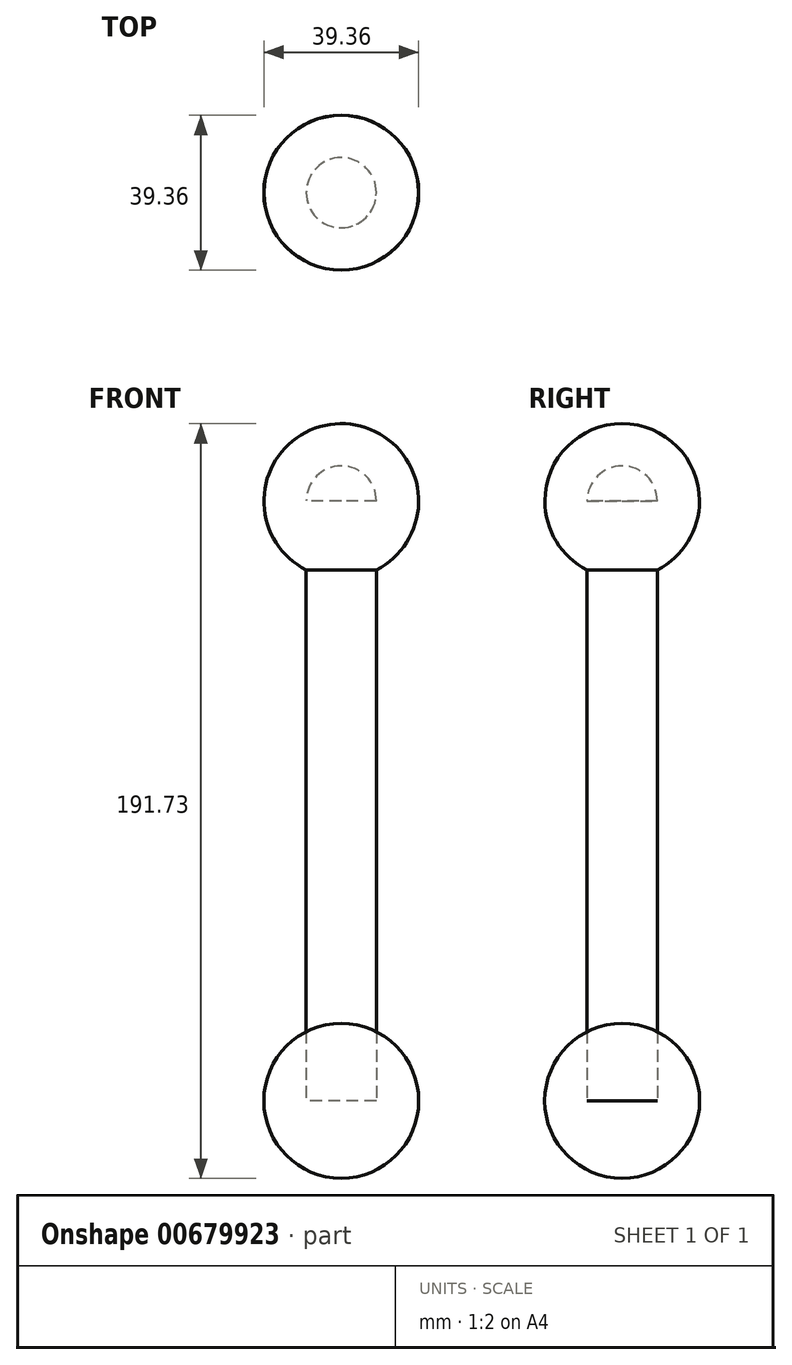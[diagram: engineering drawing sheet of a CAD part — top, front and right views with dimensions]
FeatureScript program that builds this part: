
annotation { "Feature Type Name" : "Feature", "Feature Type Description" : "" }
export const myFeature = defineFeature(function(context is Context, id is Id, definition is map)
    precondition{}
    {
        {
            var Q0;
            Q0=qCreatedBy(makeId("Top.planeOp"),FACE);
            var sketch = newSketch(context, id + "F0", { "sketchPlane" : qUnion([Q0])});
            skPoint(sketch, "E0", {"position": v(0, 0) * mm});
            skCircle(sketch, "E1", {"center": v(0, 0) * mm, "radius": 19.68 * mm});
            skSolve(sketch);
        }
        {
            var Q0;
            Q0=makeQuery(id+"F0.imprint","IMPRINT",FACE,{"disambiguationData":[TD([[makeQuery(id+"F0.imprint","IMPRINT",EDGE,{"derivedFrom":sQuery(id+"F0.wireOp",EDGE,"E1")}),1.0]])]});
            var sketch = newSketch(context, id + "F1", { "sketchPlane" : qUnion([Q0])});
            skLineSegment(sketch, "E2", {"start": v(0, -23) * mm, "end": v(0, 23.21) * mm});
            skSolve(sketch);
        }
        {
            var Q0;
            {var subQ0=sQuery(id+"F1.wireOp",EDGE,"E2");var subQ1=makeQuery(id+"F0.imprint","IMPRINT",EDGE,{"derivedFrom":sQuery(id+"F0.wireOp",EDGE,"E1")});var subQ2=makeQuery(id+"F1.imprint","INTERSECT",VERTEX,{"disambiguationData":[OD(0.0)],"derivedFrom":[subQ1,subQ0]});Q0=makeQuery(id+"F1.imprint","IMPRINT",FACE,{"disambiguationData":[TD([[makeQuery(id+"F1.imprint","IMPRINT",EDGE,{"disambiguationData":[TD([[subQ2,-1.0]])],"derivedFrom":subQ0}),-1.0]])]});}
            var sketch = newSketch(context, id + "F2", { "sketchPlane" : qUnion([Q0])});
            skSolve(sketch);
        }
        {
            var Q0;
            {var subQ0=sQuery(id+"F1.wireOp",EDGE,"E2");var subQ1=makeQuery(id+"F0.imprint","IMPRINT",EDGE,{"derivedFrom":sQuery(id+"F0.wireOp",EDGE,"E1")});var subQ2=makeQuery(id+"F1.imprint","INTERSECT",VERTEX,{"disambiguationData":[OD(0.0)],"derivedFrom":[subQ1,subQ0]});Q0=makeQuery(id+"F2.imprint","IMPRINT",FACE,{"disambiguationData":[TD([[makeQuery(id+"F2.imprint","IMPRINT",EDGE,{"derivedFrom":makeQuery(id+"F1.imprint","IMPRINT",EDGE,{"disambiguationData":[TD([[subQ2,-1.0]])],"derivedFrom":subQ0})}),-1.0]])]});}
            var sketch = newSketch(context, id + "F3", { "sketchPlane" : qUnion([Q0])});
            skLineSegment(sketch, "E3", {"start": v(0, 17.3) * mm, "end": v(0, -16.86) * mm});
            skLineSegment(sketch, "E4", {"start": v(0, -16.86) * mm, "end": v(0, -19.6) * mm});
            skLineSegment(sketch, "E5", {"start": v(0, -19.6) * mm, "end": v(0, 17.3) * mm});
            skLineSegment(sketch, "E6", {"start": v(0, 19.67) * mm, "end": v(0, 17.3) * mm});
            skSolve(sketch);
        }
        {
            var Q0;
            {var subQ0=sQuery(id+"F1.wireOp",EDGE,"E2");var subQ1=makeQuery(id+"F0.imprint","IMPRINT",EDGE,{"derivedFrom":sQuery(id+"F0.wireOp",EDGE,"E1")});var subQ2=makeQuery(id+"F1.imprint","INTERSECT",VERTEX,{"disambiguationData":[OD(0.0)],"derivedFrom":[subQ1,subQ0]});Q0=makeQuery(id+"F2.imprint","IMPRINT",FACE,{"disambiguationData":[TD([[makeQuery(id+"F2.imprint","IMPRINT",EDGE,{"derivedFrom":makeQuery(id+"F1.imprint","IMPRINT",EDGE,{"disambiguationData":[TD([[subQ2,-1.0]])],"derivedFrom":subQ0})}),-1.0]])]});}
            var Q1;
            Q1=sQuery(id+"F3.wireOp",EDGE,"E5");
            revolve(context, id + "F4", {"entities" : qUnion([Q0]), "axis" : qUnion([Q1]), "revolveType" : RevolveType.FULL});
        }
        {
            var Q0;
            Q0=qCreatedBy(makeId("Top.planeOp"),FACE);
            var sketch = newSketch(context, id + "F5", { "sketchPlane" : qUnion([Q0])});
            skCircle(sketch, "E7", {"center": v(0, 0) * mm, "radius": 8.9 * mm});
            skSolve(sketch);
        }
        {
            var Q0;
            Q0=makeQuery(id+"F5.imprint","IMPRINT",FACE,{"disambiguationData":[TD([[makeQuery(id+"F5.imprint","IMPRINT",EDGE,{"derivedFrom":sQuery(id+"F5.wireOp",EDGE,"E7")}),1.0]])]});
            extrude(context, id + "F6", {"entities" : qUnion([Q0]), "depth" : 152.4 * mm, "offsetDistance" : 25.4 * mm});
        }
        {
            var Q0;
            Q0=makeQuery(id+"F6.opExtrude","CAP_FACE",FACE,{"disambiguationData":[OSD([sQuery(id+"F5.wireOp",EDGE,"E7")])],"isStart":false});
            var sketch = newSketch(context, id + "F7", { "sketchPlane" : qUnion([Q0])});
            skArc(sketch, "E8", {"start": v(0, -19.65) * mm, "mid": v(19.65, 0) * mm, "end": v(0, 19.65) * mm});
            skLineSegment(sketch, "E9", {"start": v(0, 0) * mm, "end": v(0, 19.65) * mm});
            skLineSegment(sketch, "E10", {"start": v(0, 19.65) * mm, "end": v(0, 0) * mm});
            skLineSegment(sketch, "E11", {"start": v(0, 0) * mm, "end": v(0, -19.65) * mm});
            skSolve(sketch);
        }
        {
            var Q0;
            {var subQ0=sQuery(id+"F7.wireOp",EDGE,"E8");Q0=makeQuery(id+"F7.imprint","IMPRINT",FACE,{"disambiguationData":[TD([[makeQuery(id+"F7.imprint","IMPRINT",EDGE,{"derivedFrom":subQ0}),1.0]])]});}
            var Q1;
            {var subQ0=sQuery(id+"F7.wireOp",EDGE,"E11");var subQ1=sQuery(id+"F7.wireOp",EDGE,"E10");var subQ2=makeQuery(id+"F7.imprint","INTERSECT",VERTEX,{"derivedFrom":[subQ1,subQ0]});Q1=makeQuery(id+"F7.imprint","IMPRINT",FACE,{"disambiguationData":[TD([[makeQuery(id+"F7.imprint","IMPRINT",EDGE,{"disambiguationData":[TD([[subQ2,1.0]])],"derivedFrom":subQ1}),1.0]])]});}
            var Q2;
            Q2=sQuery(id+"F7.wireOp",EDGE,"E11");
            revolve(context, id + "F8", {"operationType" : NewBodyOperationType.ADD, "entities" : qUnion([Q0, Q1]), "axis" : qUnion([Q2]), "revolveType" : RevolveType.FULL});
        }
    });
